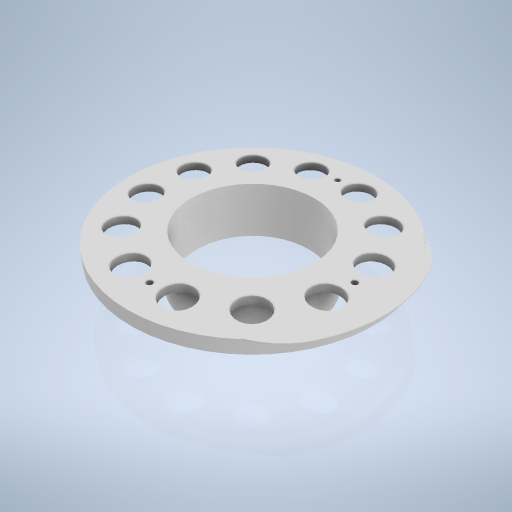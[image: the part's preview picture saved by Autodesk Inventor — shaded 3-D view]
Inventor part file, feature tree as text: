
AUTODESK INVENTOR PART (.ipt)
format: ipt  version: 2024.2 (Build 282272000, 272)  size: 363,520 bytes
history: native  units: mm
features: sketch x4, hole x2, revolve x1, pattern_circular x1, extrude x1
ambient origin geometry x8: Origin, YZ Plane, XZ Plane, XY Plane, X Axis, Y Axis, Z Axis, Center Point
bodies: Volumenkörper1 (feature_tree)
feature tree (9):
  revolve  "Umdrehung1"
  hole  "Bohrung1"  [1 undecoded]
  pattern_circular  "Runde Anordnung1"  Count=7  [1 undecoded]
  hole  "Bohrung2"  [1 undecoded]
  extrude  "Extrusion1"  Depth=1.5mm
  sketch  "Skizze1"  dims[d1=14.0mm d2=3.2mm d3=35.0mm]
  sketch  "Skizze2"  dims[d4=38.0mm d5=70.0mm]
  sketch  "Skizze3"  dims[d7=90.0deg d8=2.0mm]
  sketch  "Skizze4"  dims[d10=2.0mm d11=1.5mm d13=54.0mm d14=30.0deg d15=45.0deg d16=8.0mm d17=6.0mm d18=3.0mm d19=2.0mm d20=90.0deg d21=8.0mm d22=20.594885mm d23=120.0mm d24=360.0deg d26=1.567mm d27=4.0mm d28=4.0mm d29=2.0mm d30=90.0deg d31=8.0mm d32=0.0mm d33=54.0mm d34=69.0mm d35=1.5mm d36=3.5mm d43=74.0mm d45=0.3mm d46=0.0mm d47=19.0mm d48=20.0mm d49=19.0mm d50=20.0mm d51=50.0mm d52=80.0mm d53=24.0mm d54=26.0mm]
note: 3 required parameter values undecoded (feature->parameter linkage not recoverable at this tier; creation-order binding heuristic only, values carry confidence <= 0.55)
